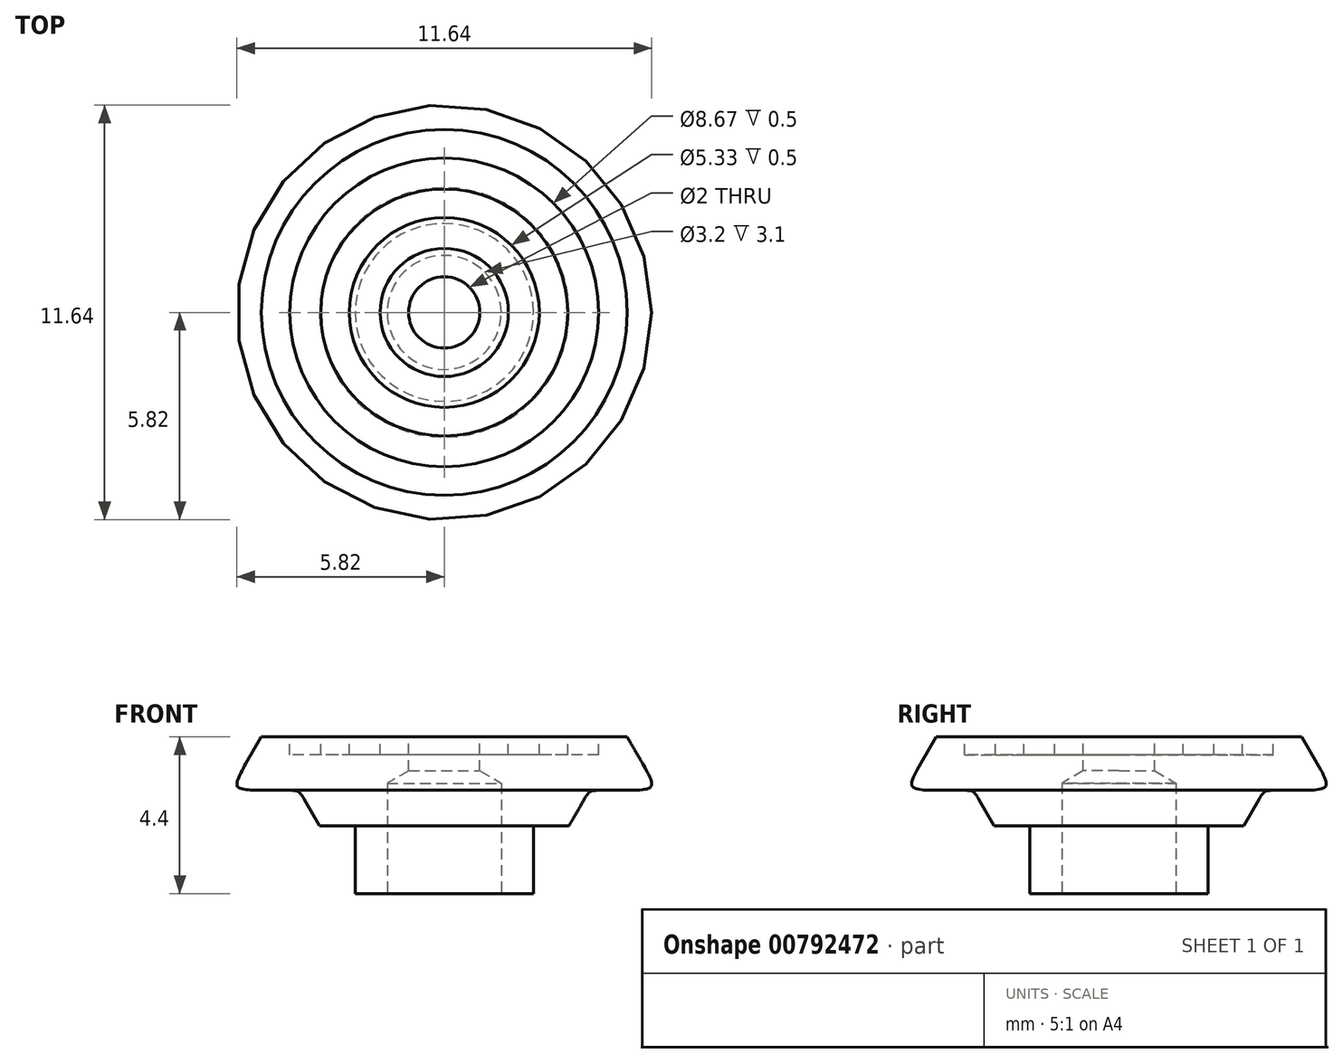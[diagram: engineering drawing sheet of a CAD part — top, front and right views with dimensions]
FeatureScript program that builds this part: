
annotation { "Feature Type Name" : "Feature", "Feature Type Description" : "" }
export const myFeature = defineFeature(function(context is Context, id is Id, definition is map)
    precondition{}
    {
        {
            var Q0;
            Q0=qCreatedBy(makeId("Right.planeOp"),FACE);
            var sketch = newSketch(context, id + "F0", { "sketchPlane" : qUnion([Q0])});
            skLineSegment(sketch, "E0", {"start": v(0, 0) * mm, "end": v(2.5, 0) * mm});
            skLineSegment(sketch, "E1", {"start": v(2.5, 0) * mm, "end": v(2.5, 1.9) * mm});
            skLineSegment(sketch, "E2", {"start": v(4.08, 2.9) * mm, "end": v(6, 2.9) * mm});
            skLineSegment(sketch, "E3", {"start": v(6, 2.9) * mm, "end": v(5.13, 4.4) * mm});
            skLineSegment(sketch, "E4", {"start": v(0, 4.4) * mm, "end": v(0, 0) * mm});
            skLineSegment(sketch, "E5", {"start": v(0, 4.4) * mm, "end": v(5.13, 4.4) * mm});
            skLineSegment(sketch, "E6", {"start": v(2.5, 1.9) * mm, "end": v(3.5, 1.9) * mm});
            skLineSegment(sketch, "E7", {"start": v(3.5, 1.9) * mm, "end": v(4.08, 2.9) * mm});
            skLineSegment(sketch, "E8", {"start": v(0, 3.9) * mm, "end": v(1, 3.9) * mm});
            skLineSegment(sketch, "E9", {"start": v(1, 3.9) * mm, "end": v(1, 4.4) * mm});
            skLineSegment(sketch, "E10", {"start": v(1.8, 4.4) * mm, "end": v(1.8, 3.9) * mm});
            skLineSegment(sketch, "E11", {"start": v(1.8, 3.9) * mm, "end": v(2.67, 3.9) * mm});
            skLineSegment(sketch, "E12", {"start": v(4.33, 3.9) * mm, "end": v(4.33, 4.4) * mm});
            skLineSegment(sketch, "E13", {"start": v(2.67, 4.4) * mm, "end": v(2.67, 3.9) * mm});
            skLineSegment(sketch, "E14", {"start": v(3.47, 4.4) * mm, "end": v(3.47, 3.9) * mm});
            skLineSegment(sketch, "E15.trimOffspring", {"start": v(3.47, 3.9) * mm, "end": v(4.33, 3.9) * mm});
            skSolve(sketch);
        }
        {
            var Q0;
            Q0=makeQuery(id+"F0.imprint","IMPRINT",FACE,{"disambiguationData":[TD([[makeQuery(id+"F0.imprint","IMPRINT",EDGE,{"derivedFrom":sQuery(id+"F0.wireOp",EDGE,"E0")}),1.0]])]});
            var Q1;
            {var subQ3=sQuery(id+"F0.wireOp",EDGE,"E6");Q1=makeQuery(id+"F0.imprint","IMPRINT",FACE,{"disambiguationData":[TD([[makeQuery(id+"F0.imprint","IMPRINT",EDGE,{"derivedFrom":subQ3}),1.0]])]});}
            var Q2;
            Q2=sQuery(id+"F0.wireOp",EDGE,"E4");
            revolve(context, id + "F1", {"surfaceOperationType" : NewSurfaceOperationType.NEW, "entities" : qUnion([Q0, Q1]), "axis" : qUnion([Q2]), "revolveType" : RevolveType.FULL});
        }
        {
            var Q0;
            Q0=makeQuery(id+"F1.opRevolve","SWEPT_EDGE",EDGE,{"disambiguationData":[OSD([sQuery(id+"F0.wireOp",EDGE,"E2"),sQuery(id+"F0.wireOp",EDGE,"E3")])]});
            var Q1;
            Q1=makeQuery(id+"F1.opRevolve","SWEPT_EDGE",EDGE,{"disambiguationData":[OSD([sQuery(id+"F0.wireOp",EDGE,"E2"),sQuery(id+"F0.wireOp",EDGE,"E7")])]});
            fillet(context, id + "F2", {"entities" : qUnion([Q0, Q1]), "radius" : .5 * mm, "tangentPropagation" : true, "rho" : .7, "crossSection" : FilletCrossSection.CONIC, "allowEdgeOverflow" : false});
        }
        {
            var Q0;
            Q0=makeQuery(id+"F1.opRevolve","SWEPT_FACE",FACE,{"disambiguationData":[OSD([sQuery(id+"F0.wireOp",EDGE,"E0")])]});
            var sketch = newSketch(context, id + "F3", { "sketchPlane" : qUnion([Q0])});
            skCircle(sketch, "E16", {"center": v(0, 0) * mm, "radius": 1.6 * mm});
            skSolve(sketch);
        }
        {
            var Q0;
            Q0=makeQuery(id+"F3.imprint","IMPRINT",FACE,{"disambiguationData":[TD([[makeQuery(id+"F3.imprint","IMPRINT",EDGE,{"derivedFrom":sQuery(id+"F3.wireOp",EDGE,"E16")}),1.0]])]});
            extrude(context, id + "F4", {"entities" : qUnion([Q0]), "operationType" : NewBodyOperationType.REMOVE, "oppositeDirection" : true, "depth" : 3.5 * mm, "offsetDistance" : 25 * mm});
        }
        {
            var Q0;
            Q0=makeQuery(id+"F4.boolean.opBoolean","COPY",EDGE,{"derivedFrom":makeQuery(id+"F4.opExtrude","CAP_EDGE",EDGE,{"disambiguationData":[OSD([sQuery(id+"F3.wireOp",EDGE,"E16")])],"isStart":false})});
            chamfer(context, id + "F5", {"entities" : qUnion([Q0]), "chamferType" : ChamferType.OFFSET_ANGLE, "width" : .4 * mm, "oppositeDirection" : true, "angle" : 60 * degree, "tangentPropagation" : true});
        }
        {
            var Q0;
            Q0=makeQuery(id+"F1.opRevolve","SWEPT_FACE",FACE,{"disambiguationData":[OSD([sQuery(id+"F0.wireOp",EDGE,"E8")])]});
            extrude(context, id + "F6", {"entities" : qUnion([Q0]), "operationType" : NewBodyOperationType.REMOVE, "endBound" : BoundingType.THROUGH_ALL, "oppositeDirection" : true, "depth" : 25 * mm, "offsetDistance" : 25 * mm});
        }
    });
